FCSTD DOCUMENT  (FreeCAD 1.0R39109 (Git))
Label: rect-to-round
License: All rights reserved
LicenseURL: http://en.wikipedia.org/wiki/All_rights_reserved
objects: Sketcher::SketchObject×2, PartDesign::Body×1
note: 5 computed .brp shape members not serialized (recipe doc carries the construction recipe); baked Part::Feature solids carry a one-line shape summary decoded from their .brp

FEATURE [PartDesign::Body] Body
  AllowCompound = false
  Origin = -> Origin
FEATURE [Sketcher::SketchObject] Sketch  label="inlet"
  ArcFitTolerance = 1e-06
  FullyConstrained = true
  MakeInternals = false
  Placement = pos=(0,0,0) rot=(0.57735,0.57735,0.57735;2.0944rad)
  sketch-geometry (5):
    g0: LineSegment StartX=-304.8 StartY=127 StartZ=0 EndX=-304.8 EndY=-127 EndZ=0
    g1: LineSegment StartX=-304.8 StartY=-127 StartZ=0 EndX=304.8 EndY=-127 EndZ=0
    g2: LineSegment StartX=304.8 StartY=-127 StartZ=0 EndX=304.8 EndY=127 EndZ=0
    g3: LineSegment StartX=304.8 StartY=127 StartZ=0 EndX=-304.8 EndY=127 EndZ=0
    g4: GeomPoint [constr] X=0 Y=0 Z=0
  constraints (12):
    c: Coincident(g0,g1)
    c: Coincident(g1,g2)
    c: Coincident(g2,g3)
    c: Coincident(g3,g0)
    c: Vertical(g0)
    c: Vertical(g2)
    c: Horizontal(g1)
    c: Horizontal(g3)
    c: Symmetric(g2,g0,g4)
    c: Coincident(g4,g-1)
    c: DistanceX(g3,g3) = 609.6
    c: DistanceY(g0,g0) = 254
FEATURE [Sketcher::SketchObject] Sketch001  label="outlet"
  ArcFitTolerance = 1e-06
  FullyConstrained = true
  MakeInternals = false
  MapMode = 4
  Placement = pos=(0,0,0) rot=(0.57735,0.57735,0.57735;2.0944rad)
  sketch-geometry (1):
    g0: Circle CenterX=0 CenterY=0 CenterZ=0 NormalX=0 NormalY=0 NormalZ=1 AngleXU=0 Radius=76.2
  constraints (2):
    c: Coincident(g0,g-1)
    c: Diameter(g0) = 152.4
